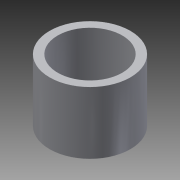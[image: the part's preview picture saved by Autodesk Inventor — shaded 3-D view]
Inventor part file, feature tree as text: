
AUTODESK INVENTOR PART (.ipt)
format: ipt  version: 2014 SP1 (Build 180222100, 222)  size: 78,848 bytes
history: native  units: in
note: dims shown in document units (in); Inventor stores cm internally (conversion verified against a paired STEP export)
features: extrude x1, sketch x1
ambient origin geometry x8: Origin, YZ Plane, XZ Plane, XY Plane, X Axis, Y Axis, Z Axis, Center Point
bodies: Solid1 (feature_tree)
feature tree (2):
  extrude  "Extrusion1"  Depth=0.3937in
  sketch  "Sketch1"  dims[d0=0.315in d1=0.3937in d2=0.3031in d3=0.0in]
